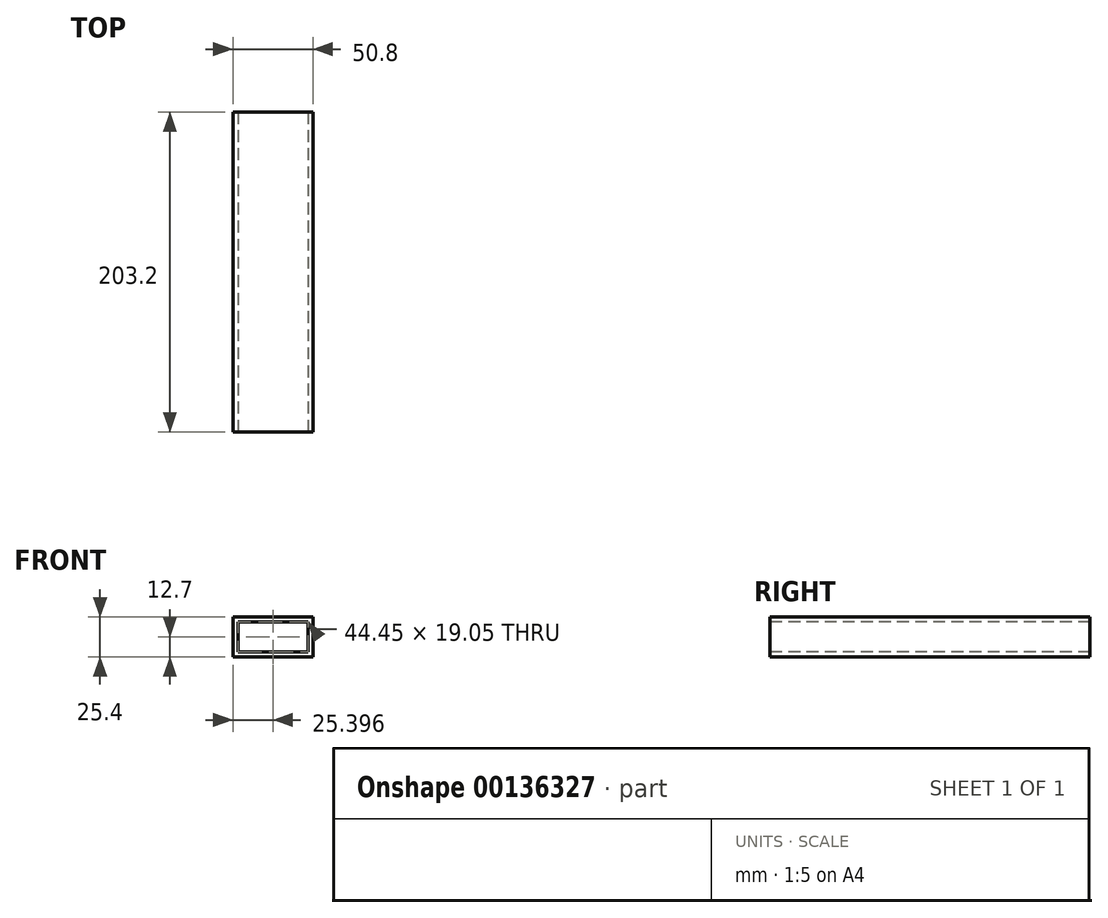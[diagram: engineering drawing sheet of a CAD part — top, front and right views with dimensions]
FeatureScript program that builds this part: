
annotation { "Feature Type Name" : "Feature", "Feature Type Description" : "" }
export const myFeature = defineFeature(function(context is Context, id is Id, definition is map)
    precondition{}
    {
        {
            var Q0;
            Q0=qCreatedBy(makeId("Top.planeOp"),FACE);
            var sketch = newSketch(context, id + "F0", { "sketchPlane" : qUnion([Q0])});
            skLineSegment(sketch, "E0.bottom", {"start": v(-22.38, 190.84) * mm, "end": v(28.42, 190.84) * mm});
            skLineSegment(sketch, "E0.top", {"start": v(-22.38, -12.36) * mm, "end": v(28.42, -12.36) * mm});
            skLineSegment(sketch, "E0.left", {"start": v(-22.38, 190.84) * mm, "end": v(-22.38, -12.36) * mm});
            skLineSegment(sketch, "E0.right", {"start": v(28.42, 190.84) * mm, "end": v(28.42, -12.36) * mm});
            skSolve(sketch);
        }
        {
            var Q0;
            Q0 = qSketchRegion(id + "F0", true);
            extrude(context, id + "F1", {"entities" : qUnion([Q0]), "depth" : 25.4 * mm});
        }
        {
            var Q0;
            Q0=makeQuery(id+"F1.opExtrude","SWEPT_FACE",FACE,{"disambiguationData":[OSD([sQuery(id+"F0.wireOp",EDGE,"E0.top")])]});
            var Q1;
            Q1=makeQuery(id+"F1.opExtrude","SWEPT_FACE",FACE,{"disambiguationData":[OSD([sQuery(id+"F0.wireOp",EDGE,"E0.bottom")])]});
            shell(context, id + "F2", {"entities" : qUnion([Q0, Q1]), "thickness" : 3.17 * mm});
        }
    });
